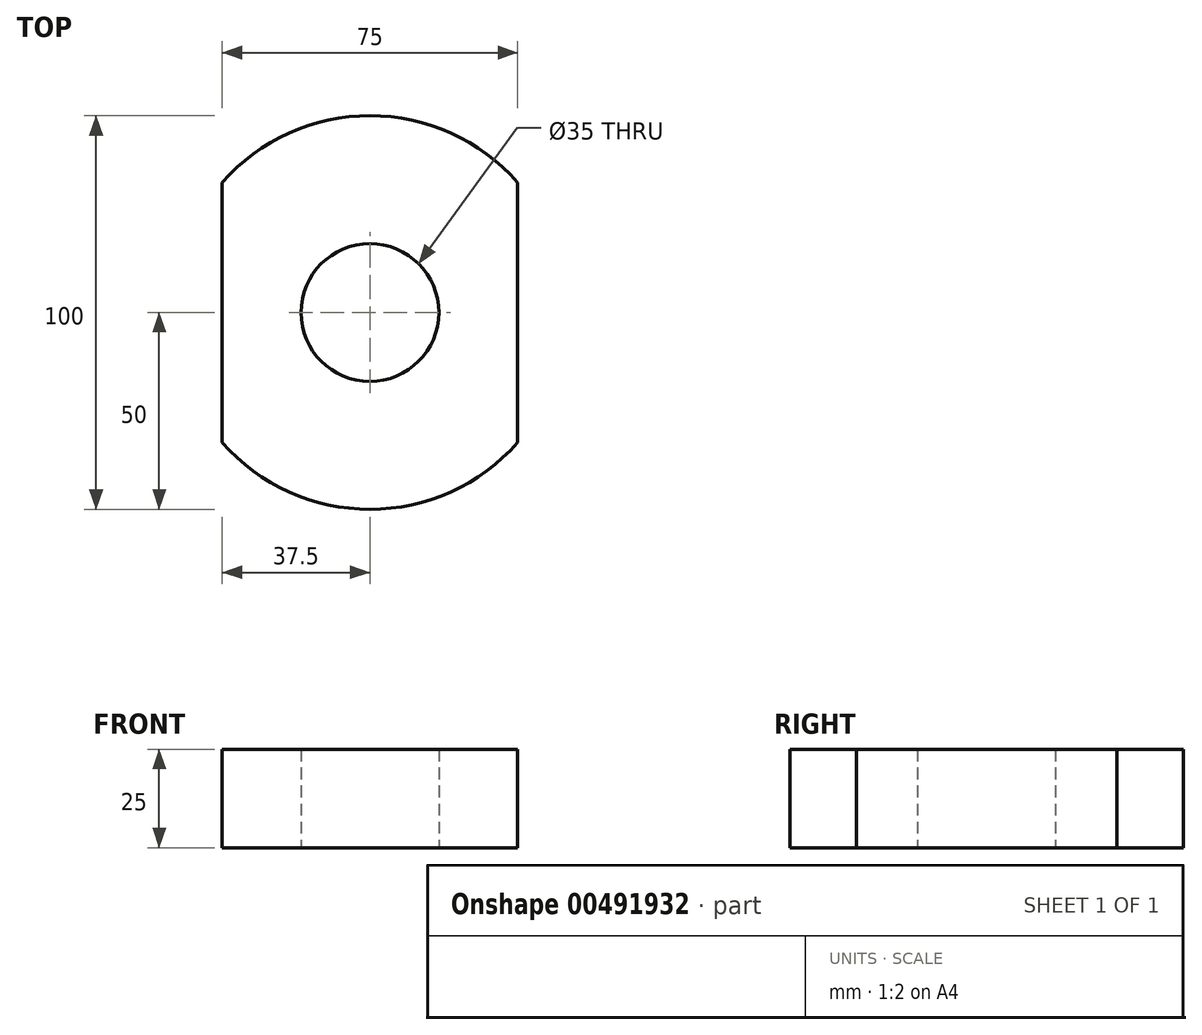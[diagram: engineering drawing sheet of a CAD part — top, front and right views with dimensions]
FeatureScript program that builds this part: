
annotation { "Feature Type Name" : "Feature", "Feature Type Description" : "" }
export const myFeature = defineFeature(function(context is Context, id is Id, definition is map)
    precondition{}
    {
        {
            var Q0;
            Q0=qCreatedBy(makeId("Top.planeOp"),FACE);
            var sketch = newSketch(context, id + "F0", { "sketchPlane" : qUnion([Q0])});
            skLineSegment(sketch, "E0.bottom", {"start": v(-37.5, -50) * mm, "end": v(37.5, -50) * mm});
            skLineSegment(sketch, "E0.top", {"start": v(-37.5, 50) * mm, "end": v(37.5, 50) * mm});
            skPoint(sketch, "E0.middle", {"position": v(0, 0) * mm});
            skPoint(sketch, "E1.endSnap0", {"position": v(0, -50) * mm});
            skPoint(sketch, "E2.endSnap0", {"position": v(0, 50) * mm});
            skLineSegment(sketch, "E3", {"start": v(-13.5, -25.5) * mm, "end": v(-37.5, -25.5) * mm});
            skLineSegment(sketch, "E4", {"start": v(-13.5, -25.5) * mm, "end": v(-13.5, -37.5) * mm});
            skLineSegment(sketch, "E5", {"start": v(-13.5, -37.5) * mm, "end": v(-37.5, -37.5) * mm});
            skLineSegment(sketch, "E6", {"start": v(-37.5, -37.5) * mm, "end": v(-37.5, -50) * mm});
            skLineSegment(sketch, "E7", {"start": v(-37.5, 0) * mm, "end": v(-37.5, -25.5) * mm});
            skLineSegment(sketch, "E8", {"start": v(-37.5, -25.5) * mm, "end": v(-37.5, -37.5) * mm});
            skLineSegment(sketch, "E9", {"start": v(-37.5, 50) * mm, "end": v(-37.5, 37.5) * mm});
            skLineSegment(sketch, "E10", {"start": v(-37.5, 37.5) * mm, "end": v(-37.5, 25.5) * mm});
            skLineSegment(sketch, "E11", {"start": v(-37.5, 25.5) * mm, "end": v(-37.5, 0) * mm});
            skLineSegment(sketch, "E12", {"start": v(37.5, 50) * mm, "end": v(37.5, 37.5) * mm});
            skLineSegment(sketch, "E13", {"start": v(37.5, 37.5) * mm, "end": v(37.5, 25.5) * mm});
            skLineSegment(sketch, "E14", {"start": v(37.5, -37.5) * mm, "end": v(37.5, -50) * mm});
            skLineSegment(sketch, "E15", {"start": v(-37.5, 25.5) * mm, "end": v(-13.5, 25.5) * mm});
            skLineSegment(sketch, "E16", {"start": v(-13.5, 25.5) * mm, "end": v(-13.5, 37.5) * mm});
            skLineSegment(sketch, "E17", {"start": v(-13.5, 37.5) * mm, "end": v(-37.5, 37.5) * mm});
            skLineSegment(sketch, "E18", {"start": v(37.5, 37.5) * mm, "end": v(13.5, 37.5) * mm});
            skLineSegment(sketch, "E19", {"start": v(13.5, 37.5) * mm, "end": v(13.5, 25.5) * mm});
            skLineSegment(sketch, "E20", {"start": v(13.5, -37.5) * mm, "end": v(37.5, -37.5) * mm});
            skLineSegment(sketch, "E21", {"start": v(37.5, 25.5) * mm, "end": v(13.5, 25.5) * mm});
            skLineSegment(sketch, "E22", {"start": v(37.5, 25.5) * mm, "end": v(37.5, 0) * mm});
            skLineSegment(sketch, "E23", {"start": v(37.5, -37.5) * mm, "end": v(37.5, -26) * mm});
            skLineSegment(sketch, "E24", {"start": v(37.5, -26) * mm, "end": v(13.5, -26) * mm});
            skLineSegment(sketch, "E25", {"start": v(13.5, -26) * mm, "end": v(13.5, -37.5) * mm});
            skLineSegment(sketch, "E26", {"start": v(37.5, -26) * mm, "end": v(37.5, 0) * mm});
            skCircle(sketch, "E27", {"center": v(0, 0) * mm, "radius": 50 * mm});
            skCircle(sketch, "E28", {"center": v(0, 0) * mm, "radius": 17.5 * mm});
            skSolve(sketch);
        }
        {
            var Q0;
            Q0=makeQuery(id+"F0.imprint","IMPRINT",FACE,{"disambiguationData":[TD([[makeQuery(id+"F0.imprint","IMPRINT",EDGE,{"derivedFrom":sQuery(id+"F0.wireOp",EDGE,"E3")}),-1.0]])]});
            var Q1;
            {var subQ4=sQuery(id+"F0.wireOp",EDGE,"E15");Q1=makeQuery(id+"F0.imprint","IMPRINT",FACE,{"disambiguationData":[TD([[makeQuery(id+"F0.imprint","IMPRINT",EDGE,{"derivedFrom":subQ4}),1.0]])]});}
            var Q2;
            {var subQ4=sQuery(id+"F0.wireOp",EDGE,"E19");Q2=makeQuery(id+"F0.imprint","IMPRINT",FACE,{"disambiguationData":[TD([[makeQuery(id+"F0.imprint","IMPRINT",EDGE,{"derivedFrom":subQ4}),1.0]])]});}
            var Q3;
            {var subQ1=sQuery(id+"F0.wireOp",EDGE,"E24");Q3=makeQuery(id+"F0.imprint","IMPRINT",FACE,{"disambiguationData":[TD([[makeQuery(id+"F0.imprint","IMPRINT",EDGE,{"derivedFrom":subQ1}),1.0]])]});}
            var Q4;
            {var subQ5=sQuery(id+"F0.wireOp",EDGE,"E3");Q4=makeQuery(id+"F0.imprint","IMPRINT",FACE,{"disambiguationData":[TD([[makeQuery(id+"F0.imprint","IMPRINT",EDGE,{"derivedFrom":subQ5}),1.0]])]});}
            extrude(context, id + "F1", {"entities" : qUnion([Q0, Q1, Q2, Q3, Q4]), "depth" : 25 * mm});
        }
    });
